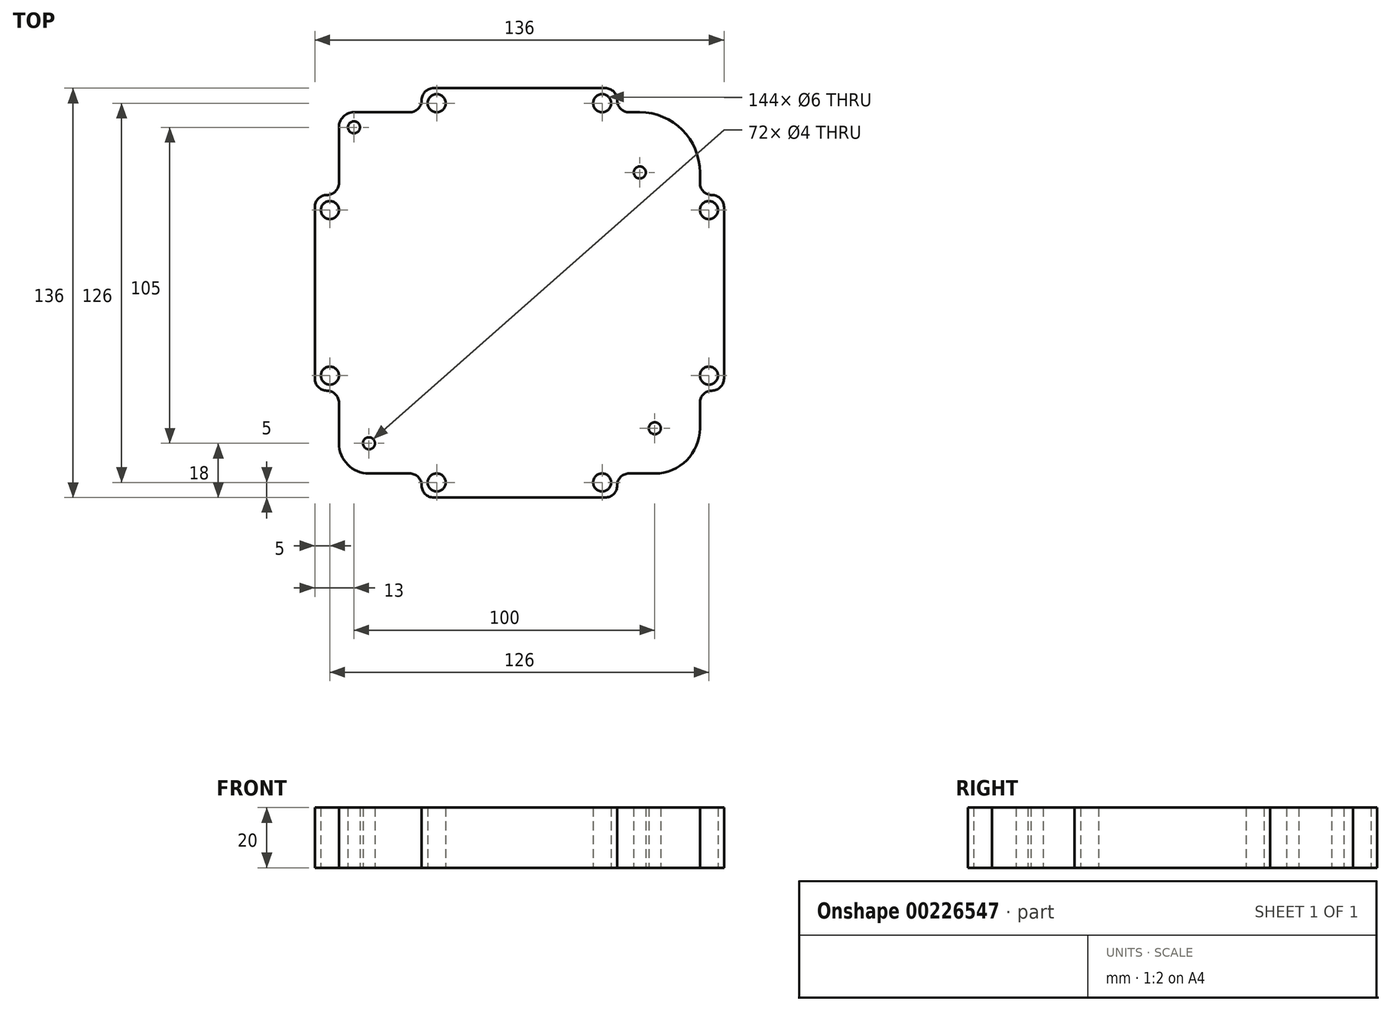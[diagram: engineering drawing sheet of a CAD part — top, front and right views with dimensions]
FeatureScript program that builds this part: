
annotation { "Feature Type Name" : "Feature", "Feature Type Description" : "" }
export const myFeature = defineFeature(function(context is Context, id is Id, definition is map)
    precondition{}
    {
        {
            var Q0;
            Q0=qCreatedBy(makeId("Top.planeOp"),FACE);
            var sketch = newSketch(context, id + "F0", { "sketchPlane" : qUnion([Q0])});
            skLineSegment(sketch, "E0.bottom", {"start": v(-55, 60) * mm, "end": v(-32.5, 60) * mm});
            skLineSegment(sketch, "E0.top", {"start": v(-50, -60) * mm, "end": v(-32.5, -60) * mm});
            skLineSegment(sketch, "E0.left", {"start": v(-60, 55) * mm, "end": v(-60, 32.5) * mm});
            skLineSegment(sketch, "E0.right", {"start": v(60, 40) * mm, "end": v(60, 32.5) * mm});
            skPoint(sketch, "E1.visualSharp", {"position": v(-60, 60) * mm});
            skArc(sketch, "E1.filletArc", {"start": v(-55, 60) * mm, "mid": v(-58.54, 58.54) * mm, "end": v(-60, 55) * mm});
            skPoint(sketch, "E2.visualSharp", {"position": v(-60, -60) * mm});
            skArc(sketch, "E2.filletArc", {"start": v(-60, -50) * mm, "mid": v(-57.07, -57.07) * mm, "end": v(-50, -60) * mm});
            skPoint(sketch, "E3.visualSharp", {"position": v(60, -60) * mm});
            skArc(sketch, "E3.filletArc", {"start": v(45, -60) * mm, "mid": v(55.6, -55.6) * mm, "end": v(60, -45) * mm});
            skPoint(sketch, "E4.visualSharp", {"position": v(60, 60) * mm});
            skArc(sketch, "E4.filletArc", {"start": v(60, 40) * mm, "mid": v(54.14, 54.14) * mm, "end": v(40, 60) * mm});
            skLineSegment(sketch, "E5.top", {"start": v(-32.5, 68) * mm, "end": v(32.5, 68) * mm});
            skLineSegment(sketch, "E5.left", {"start": v(-32.5, 60) * mm, "end": v(-32.5, 68) * mm});
            skLineSegment(sketch, "E5.right", {"start": v(32.5, 60) * mm, "end": v(32.5, 68) * mm});
            skLineSegment(sketch, "E6.bottom", {"start": v(-60, -32.5) * mm, "end": v(-68, -32.5) * mm});
            skLineSegment(sketch, "E6.top", {"start": v(-60, 32.5) * mm, "end": v(-68, 32.5) * mm});
            skLineSegment(sketch, "E6.right", {"start": v(-68, 32.5) * mm, "end": v(-68, -32.5) * mm});
            skLineSegment(sketch, "E7.bottom", {"start": v(60, -32.5) * mm, "end": v(68, -32.5) * mm});
            skLineSegment(sketch, "E7.top", {"start": v(60, 32.5) * mm, "end": v(68, 32.5) * mm});
            skLineSegment(sketch, "E7.right", {"start": v(68, -32.5) * mm, "end": v(68, 32.5) * mm});
            skLineSegment(sketch, "E8.top", {"start": v(-32.5, -68) * mm, "end": v(32.5, -68) * mm});
            skLineSegment(sketch, "E8.left", {"start": v(-32.5, -60) * mm, "end": v(-32.5, -68) * mm});
            skLineSegment(sketch, "E8.right", {"start": v(32.5, -60) * mm, "end": v(32.5, -68) * mm});
            skLineSegment(sketch, "E9.trimOffspring", {"start": v(-60, -32.5) * mm, "end": v(-60, -50) * mm});
            skLineSegment(sketch, "E10.trimOffspring", {"start": v(32.5, 60) * mm, "end": v(40, 60) * mm});
            skLineSegment(sketch, "E11.trimOffspring", {"start": v(60, -32.5) * mm, "end": v(60, -45) * mm});
            skLineSegment(sketch, "E12.trimOffspring", {"start": v(32.5, -60) * mm, "end": v(45, -60) * mm});
            skPoint(sketch, "E13.startSnap0", {"position": v(-32.5, -64) * mm});
            skLineSegment(sketch, "E14", {"start": v(-32.5, -62.12) * mm, "end": v(32.5, -62.12) * mm, "construction": true});
            skCircle(sketch, "E15", {"center": v(-63, 27.5) * mm, "radius": 3 * mm});
            skCircle(sketch, "E16", {"center": v(-27.5, 63) * mm, "radius": 3 * mm});
            skCircle(sketch, "E17.MirrorC", {"center": v(-63, -27.5) * mm, "radius": 3 * mm});
            skCircle(sketch, "E18.MirrorC", {"center": v(27.5, 63) * mm, "radius": 3 * mm});
            skCircle(sketch, "E19.MirrorC", {"center": v(-27.5, -63) * mm, "radius": 3 * mm});
            skCircle(sketch, "E20.MirrorC", {"center": v(27.5, -63) * mm, "radius": 3 * mm});
            skCircle(sketch, "E21.MirrorC", {"center": v(63, 27.5) * mm, "radius": 3 * mm});
            skCircle(sketch, "E22.MirrorC", {"center": v(63, -27.5) * mm, "radius": 3 * mm});
            skCircle(sketch, "E23", {"center": v(-55, 55) * mm, "radius": 2 * mm});
            skCircle(sketch, "E24", {"center": v(40, 40) * mm, "radius": 2 * mm});
            skCircle(sketch, "E25", {"center": v(45, -45) * mm, "radius": 2 * mm});
            skCircle(sketch, "E26", {"center": v(-50, -50) * mm, "radius": 2 * mm});
            skSolve(sketch);
        }
        {
            var Q0;
            Q0 = qSketchRegion(id + "F0", true);
            extrude(context, id + "F1", {"entities" : qUnion([Q0]), "depth" : 20 * mm});
        }
        {
            var Q0;
            Q0=makeQuery(id+"F1.opExtrude","SWEPT_EDGE",EDGE,{"disambiguationData":[OSD([sQuery(id+"F0.wireOp",EDGE,"E0.left"),sQuery(id+"F0.wireOp",EDGE,"E6.top")])]});
            var Q1;
            Q1=makeQuery(id+"F1.opExtrude","SWEPT_EDGE",EDGE,{"disambiguationData":[OSD([sQuery(id+"F0.wireOp",EDGE,"E6.top"),sQuery(id+"F0.wireOp",EDGE,"E6.right")])]});
            var Q2;
            Q2=makeQuery(id+"F1.opExtrude","SWEPT_EDGE",EDGE,{"disambiguationData":[OSD([sQuery(id+"F0.wireOp",EDGE,"E0.bottom"),sQuery(id+"F0.wireOp",EDGE,"E5.left")])]});
            var Q3;
            Q3=makeQuery(id+"F1.opExtrude","SWEPT_EDGE",EDGE,{"disambiguationData":[OSD([sQuery(id+"F0.wireOp",EDGE,"E5.top"),sQuery(id+"F0.wireOp",EDGE,"E5.left")])]});
            var Q4;
            Q4=makeQuery(id+"F1.opExtrude","SWEPT_EDGE",EDGE,{"disambiguationData":[OSD([sQuery(id+"F0.wireOp",EDGE,"E5.top"),sQuery(id+"F0.wireOp",EDGE,"E5.right")])]});
            var Q5;
            Q5=makeQuery(id+"F1.opExtrude","SWEPT_EDGE",EDGE,{"disambiguationData":[OSD([sQuery(id+"F0.wireOp",EDGE,"E6.bottom"),sQuery(id+"F0.wireOp",EDGE,"E6.right")])]});
            var Q6;
            Q6=makeQuery(id+"F1.opExtrude","SWEPT_EDGE",EDGE,{"disambiguationData":[OSD([sQuery(id+"F0.wireOp",EDGE,"E8.top"),sQuery(id+"F0.wireOp",EDGE,"E8.left")])]});
            var Q7;
            Q7=makeQuery(id+"F1.opExtrude","SWEPT_EDGE",EDGE,{"disambiguationData":[OSD([sQuery(id+"F0.wireOp",EDGE,"E7.bottom"),sQuery(id+"F0.wireOp",EDGE,"E11.trimOffspring")])]});
            var Q8;
            Q8=makeQuery(id+"F1.opExtrude","SWEPT_EDGE",EDGE,{"disambiguationData":[OSD([sQuery(id+"F0.wireOp",EDGE,"E7.bottom"),sQuery(id+"F0.wireOp",EDGE,"E7.right")])]});
            var Q9;
            Q9=makeQuery(id+"F1.opExtrude","SWEPT_EDGE",EDGE,{"disambiguationData":[OSD([sQuery(id+"F0.wireOp",EDGE,"E7.top"),sQuery(id+"F0.wireOp",EDGE,"E7.right")])]});
            var Q10;
            Q10=makeQuery(id+"F1.opExtrude","SWEPT_EDGE",EDGE,{"disambiguationData":[OSD([sQuery(id+"F0.wireOp",EDGE,"E8.right"),sQuery(id+"F0.wireOp",EDGE,"E12.trimOffspring")])]});
            var Q11;
            Q11=makeQuery(id+"F1.opExtrude","SWEPT_EDGE",EDGE,{"disambiguationData":[OSD([sQuery(id+"F0.wireOp",EDGE,"E8.top"),sQuery(id+"F0.wireOp",EDGE,"E8.right")])]});
            var Q12;
            Q12=makeQuery(id+"F1.opExtrude","SWEPT_EDGE",EDGE,{"disambiguationData":[OSD([sQuery(id+"F0.wireOp",EDGE,"E6.bottom"),sQuery(id+"F0.wireOp",EDGE,"E9.trimOffspring")])]});
            var Q13;
            Q13=makeQuery(id+"F1.opExtrude","SWEPT_EDGE",EDGE,{"disambiguationData":[OSD([sQuery(id+"F0.wireOp",EDGE,"E0.top"),sQuery(id+"F0.wireOp",EDGE,"E8.left")])]});
            var Q14;
            Q14=makeQuery(id+"F1.opExtrude","SWEPT_EDGE",EDGE,{"disambiguationData":[OSD([sQuery(id+"F0.wireOp",EDGE,"E0.right"),sQuery(id+"F0.wireOp",EDGE,"E7.top")])]});
            var Q15;
            Q15=makeQuery(id+"F1.opExtrude","SWEPT_EDGE",EDGE,{"disambiguationData":[OSD([sQuery(id+"F0.wireOp",EDGE,"E5.right"),sQuery(id+"F0.wireOp",EDGE,"E10.trimOffspring")])]});
            fillet(context, id + "F2", {"entities" : qUnion([Q0, Q1, Q2, Q3, Q4, Q5, Q6, Q7, Q8, Q9, Q10, Q11, Q12, Q13, Q14, Q15]), "radius" : 4 * mm, "tangentPropagation" : true, "allowEdgeOverflow" : false});
        }
    });
